# Revit family: Führungsklammer-Set, Typ 2B (I-II)
name_source: partatom
category: HLS-Bauteile
revit_build: Autodesk Revit 2018 (Build: 20190510_1515(x64)
units: mm (PartAtom-declared; Revit-internal decimal feet)

## family parameters
Arbeitsebenenbasiert = Ja
Beim Laden mit Abzugskörper schneiden = Nein
Bemaßung runder Anschluss = Durchmesser verwenden
Gemeinsam genutzt = Ja
Immer vertikal = Nein
Raumberechnungspunkt = Nein
Teiletyp = Normal

## types (2) — shared parameters
Fabrikat = MEFA
Firma = MEFA Befestigungs- und Montagesysteme GmbH
Kurztext1 = Loslager ohne Abhebesicherung mit Gleitunterlage
Material = Stahl
Materialname = S235
Mengeneinheit = St
Oberflaeche = feuerstückverzinkt
Vorgabe-Ansicht = 1219 mm
max. zul. Schublast = 4.00 kN
vpe = 1 St

## per-type parameters (varying)
| type | Artikelnummer | Faktor1 | Gewicht | Gewicht pro Bauteil | Gewindestangentyp | Klemmweite | Klemmweite Flansch max. | Klemmweite Flansch min. | Kurztext2 | Typ | min. Klemmdicke |
| Loslager ohne Abheb. mit Gleitunt., Typ 2B II | 14711005 | 85 mm  [stored 0.278871 ft] | 2.13 kg | 2.13 kg | M12 x 270 | HEA160-180, HEB140-160, IPE270-330, IPEa300-360, IPEo270-330 | 180 mm  [stored 0.590551 ft] | 160 mm  [stored 0.524934 ft] | Typ 2B II Klemmdicke 9 - 13 mm | 2B II | 9 mm |
| Loslager ohne Abheb. mit Gleitunt., Typ 2B I | 14711004 | 5 mm  [stored 0.0164042 ft] | 2.06 kg | 2.06 kg | M12 x 220 | HEA 100-140, HEB100-120, IPE200-240, IPEa240-270, IPEo200-240 | 140 mm  [stored 0.459318 ft] | 100 mm  [stored 0.328084 ft] | Typ 2B I | 2B I | 5.2 mm |

note: [stored X ft] marks values corroborated as IEEE doubles in the binary element streams (Revit-internal decimal feet)

## geometry (parser evidence)
native form markers: Sweep x3
no freeform markers — native parametric forms only
